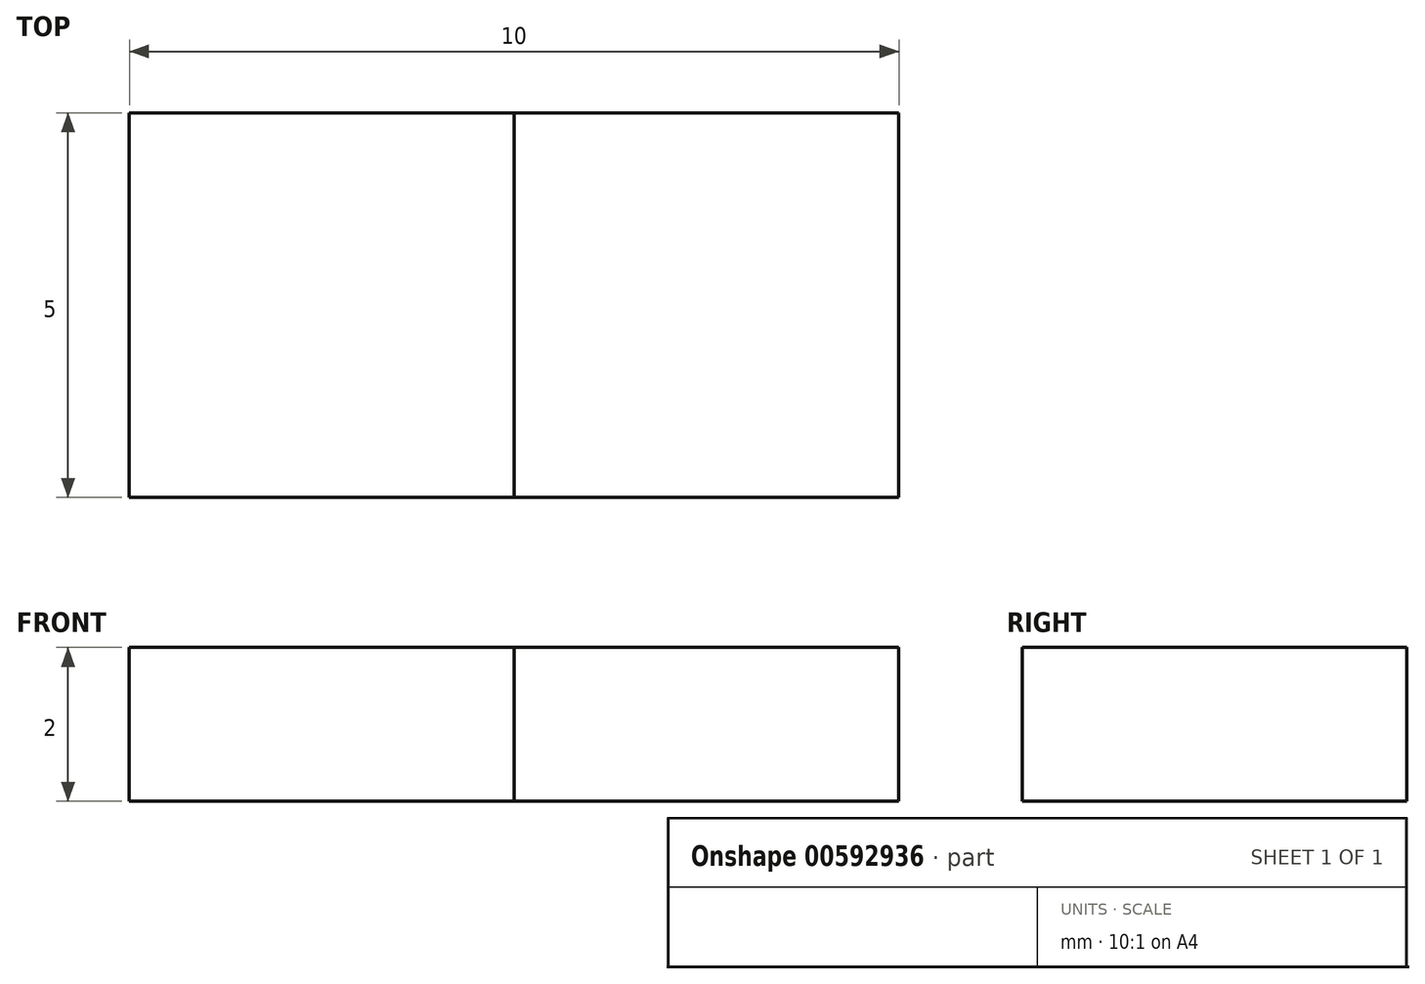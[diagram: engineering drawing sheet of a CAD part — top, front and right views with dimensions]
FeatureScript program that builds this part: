
annotation { "Feature Type Name" : "Feature", "Feature Type Description" : "" }
export const myFeature = defineFeature(function(context is Context, id is Id, definition is map)
    precondition{}
    {
        {
            var Q0;
            Q0=qCreatedBy(makeId("Top.planeOp"),FACE);
            var sketch = newSketch(context, id + "F0", { "sketchPlane" : qUnion([Q0])});
            skLineSegment(sketch, "E0.bottom", {"start": v(-10.4, 0.05) * mm, "end": v(-5.4, 0.05) * mm});
            skLineSegment(sketch, "E0.top", {"start": v(-10.4, -4.95) * mm, "end": v(-5.4, -4.95) * mm});
            skLineSegment(sketch, "E0.left", {"start": v(-10.4, 0.05) * mm, "end": v(-10.4, -4.95) * mm});
            skLineSegment(sketch, "E0.right", {"start": v(-5.4, 0.05) * mm, "end": v(-5.4, -4.95) * mm});
            skLineSegment(sketch, "E1.bottom", {"start": v(-5.4, 0.05) * mm, "end": v(-0.4, 0.05) * mm});
            skLineSegment(sketch, "E1.top", {"start": v(-5.4, -4.95) * mm, "end": v(-0.4, -4.95) * mm});
            skLineSegment(sketch, "E1.right", {"start": v(-0.4, 0.05) * mm, "end": v(-0.4, -4.95) * mm});
            skSolve(sketch);
        }
        {
            var Q0;
            Q0=makeQuery(id+"F0.imprint","IMPRINT",FACE,{"disambiguationData":[TD([[makeQuery(id+"F0.imprint","IMPRINT",EDGE,{"derivedFrom":sQuery(id+"F0.wireOp",EDGE,"E0.bottom")}),-1.0]])]});
            extrude(context, id + "F1", {"entities" : qUnion([Q0]), "depth" : 2 * mm, "offsetDistance" : 25 * mm});
        }
        {
            var Q0;
            Q0=makeQuery(id+"F0.imprint","IMPRINT",FACE,{"disambiguationData":[TD([[makeQuery(id+"F0.imprint","IMPRINT",EDGE,{"derivedFrom":sQuery(id+"F0.wireOp",EDGE,"E1.bottom")}),-1.0]])]});
            extrude(context, id + "F2", {"entities" : qUnion([Q0]), "depth" : 2 * mm, "offsetDistance" : 25 * mm});
        }
    });
